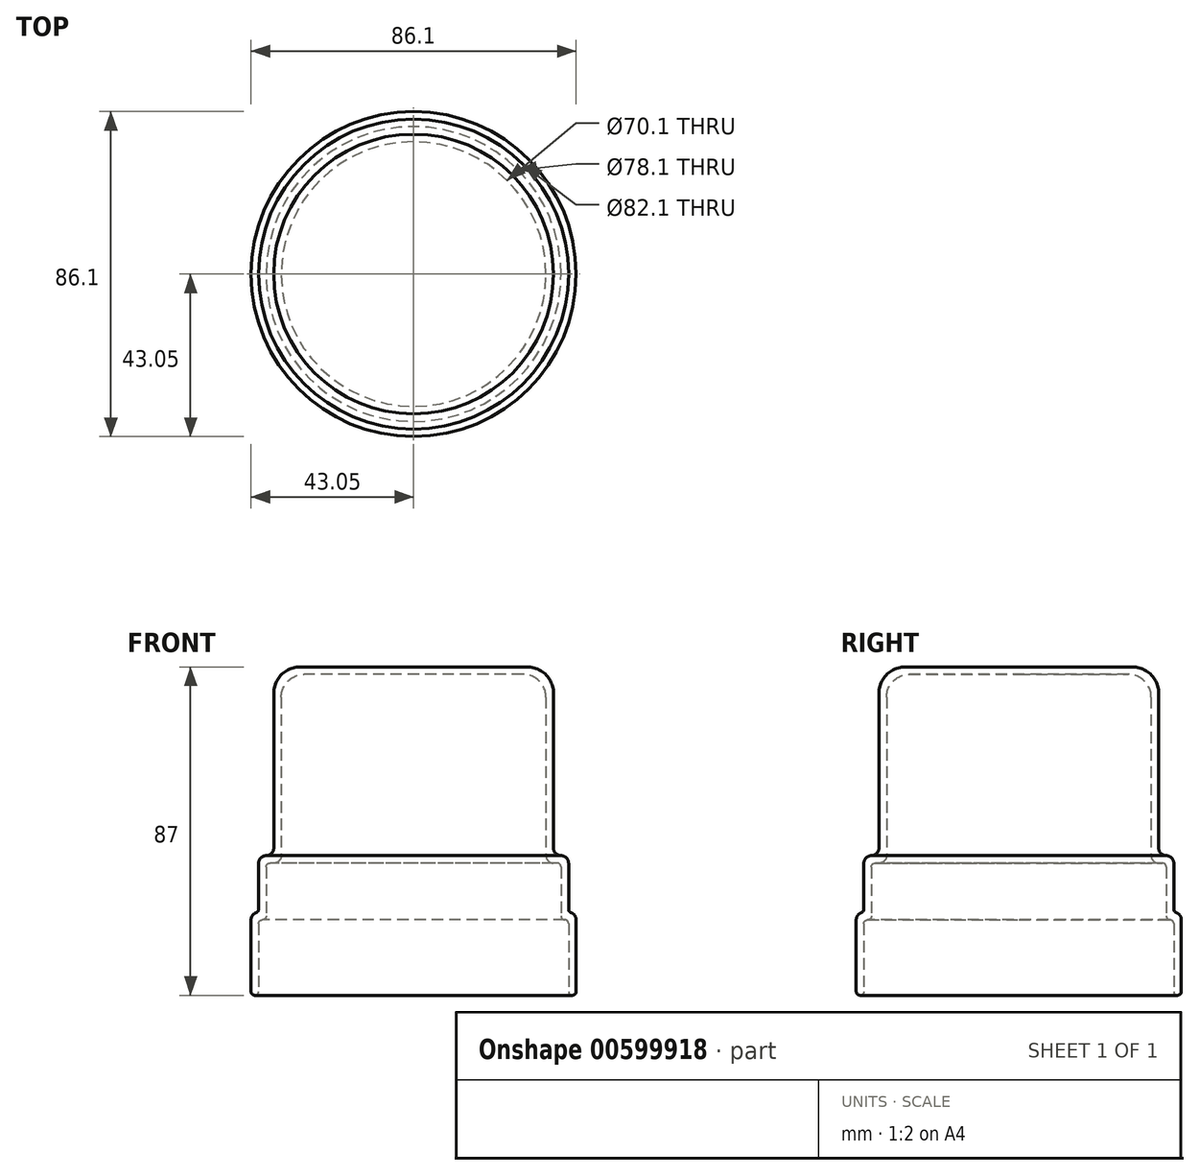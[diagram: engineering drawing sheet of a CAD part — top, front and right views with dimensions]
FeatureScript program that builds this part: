
annotation { "Feature Type Name" : "Feature", "Feature Type Description" : "" }
export const myFeature = defineFeature(function(context is Context, id is Id, definition is map)
    precondition{}
    {
        {
            var Q0;
            Q0=qCreatedBy(makeId("Front.planeOp"),FACE);
            var sketch = newSketch(context, id + "F0", { "sketchPlane" : qUnion([Q0])});
            skLineSegment(sketch, "E0", {"start": v(41.05, -10) * mm, "end": v(41.05, 10) * mm});
            skLineSegment(sketch, "E1", {"start": v(41.05, 10) * mm, "end": v(39.05, 10) * mm});
            skLineSegment(sketch, "E2", {"start": v(39.05, 10) * mm, "end": v(39.05, 25) * mm});
            skLineSegment(sketch, "E3", {"start": v(39.05, 25) * mm, "end": v(35.05, 25) * mm});
            skLineSegment(sketch, "E4", {"start": v(35.05, 25) * mm, "end": v(35.05, 75) * mm});
            skLineSegment(sketch, "E5", {"start": v(35.05, 75) * mm, "end": v(0, 75) * mm});
            skLineSegment(sketch, "E6.0", {"start": v(37.05, 77) * mm, "end": v(0, 77) * mm});
            skLineSegment(sketch, "E6.1", {"start": v(37.05, 27) * mm, "end": v(37.05, 77) * mm});
            skLineSegment(sketch, "E6.2", {"start": v(43.05, -10) * mm, "end": v(43.05, 12) * mm});
            skLineSegment(sketch, "E6.3", {"start": v(43.05, 12) * mm, "end": v(41.05, 12) * mm});
            skLineSegment(sketch, "E6.4", {"start": v(41.05, 12) * mm, "end": v(41.05, 27) * mm});
            skLineSegment(sketch, "E6.5", {"start": v(41.05, 27) * mm, "end": v(37.05, 27) * mm});
            skLineSegment(sketch, "E7", {"start": v(41.05, -10) * mm, "end": v(43.05, -10) * mm});
            skLineSegment(sketch, "E8", {"start": v(0, 75) * mm, "end": v(0, 77) * mm});
            skSolve(sketch);
        }
        {
            var Q0;
            Q0=makeQuery(id+"F0.imprint","IMPRINT",FACE,{"disambiguationData":[TD([[makeQuery(id+"F0.imprint","IMPRINT",EDGE,{"derivedFrom":sQuery(id+"F0.wireOp",EDGE,"E0")}),-1.0]])]});
            var Q1;
            Q1=sQuery(id+"F0.wireOp",EDGE,"E8");
            revolve(context, id + "F1", {"entities" : qUnion([Q0]), "axis" : qUnion([Q1]), "revolveType" : RevolveType.FULL});
        }
        {
            var Q0;
            Q0=makeQuery(id+"F1.opRevolve","SWEPT_EDGE",EDGE,{"disambiguationData":[OSD([sQuery(id+"F0.wireOp",EDGE,"E4"),sQuery(id+"F0.wireOp",EDGE,"E5")])]});
            fillet(context, id + "F2", {"entities" : qUnion([Q0]), "radius" : 6 * mm, "tangentPropagation" : true, "allowEdgeOverflow" : false});
        }
        {
            var Q0;
            Q0=makeQuery(id+"F1.opRevolve","SWEPT_EDGE",EDGE,{"disambiguationData":[OSD([sQuery(id+"F0.wireOp",EDGE,"E6.0"),sQuery(id+"F0.wireOp",EDGE,"E6.1")])]});
            fillet(context, id + "F3", {"entities" : qUnion([Q0]), "radius" : 7 * mm, "tangentPropagation" : true, "allowEdgeOverflow" : false});
        }
        {
            var Q0;
            Q0=makeQuery(id+"F1.opRevolve","SWEPT_EDGE",EDGE,{"disambiguationData":[OSD([sQuery(id+"F0.wireOp",EDGE,"E6.1"),sQuery(id+"F0.wireOp",EDGE,"E6.5")])]});
            var Q1;
            Q1=makeQuery(id+"F1.opRevolve","SWEPT_EDGE",EDGE,{"disambiguationData":[OSD([sQuery(id+"F0.wireOp",EDGE,"E6.2"),sQuery(id+"F0.wireOp",EDGE,"E6.3")])]});
            var Q2;
            Q2=makeQuery(id+"F1.opRevolve","SWEPT_EDGE",EDGE,{"disambiguationData":[OSD([sQuery(id+"F0.wireOp",EDGE,"E3"),sQuery(id+"F0.wireOp",EDGE,"E4")])]});
            fillet(context, id + "F4", {"entities" : qUnion([Q0, Q1, Q2]), "radius" : 2 * mm, "tangentPropagation" : true, "allowEdgeOverflow" : false});
        }
        {
            var Q0;
            Q0=makeQuery(id+"F1.opRevolve","SWEPT_EDGE",EDGE,{"disambiguationData":[OSD([sQuery(id+"F0.wireOp",EDGE,"E2"),sQuery(id+"F0.wireOp",EDGE,"E3")])]});
            var Q1;
            Q1=makeQuery(id+"F1.opRevolve","SWEPT_EDGE",EDGE,{"disambiguationData":[OSD([sQuery(id+"F0.wireOp",EDGE,"E0"),sQuery(id+"F0.wireOp",EDGE,"E1")])]});
            var Q2;
            Q2=makeQuery(id+"F1.opRevolve","SWEPT_EDGE",EDGE,{"disambiguationData":[OSD([sQuery(id+"F0.wireOp",EDGE,"E6.2"),sQuery(id+"F0.wireOp",EDGE,"E7")])]});
            var Q3;
            Q3=makeQuery(id+"F1.opRevolve","SWEPT_EDGE",EDGE,{"disambiguationData":[OSD([sQuery(id+"F0.wireOp",EDGE,"E0"),sQuery(id+"F0.wireOp",EDGE,"E7")])]});
            var Q4;
            Q4=makeQuery(id+"F4.opFillet","BLEND_EDGE",EDGE,{"blendedFrom":[makeQuery(id+"F1.opRevolve","SWEPT_EDGE",EDGE,{"disambiguationData":[OSD([sQuery(id+"F0.wireOp",EDGE,"E6.2"),sQuery(id+"F0.wireOp",EDGE,"E6.3")])]}),makeQuery(id+"F1.opRevolve","SWEPT_FACE",FACE,{"disambiguationData":[OSD([sQuery(id+"F0.wireOp",EDGE,"E6.4")])]})],"blendedInto":[makeQuery(id+"F1.opRevolve","SWEPT_FACE",FACE,{"disambiguationData":[OSD([sQuery(id+"F0.wireOp",EDGE,"E6.4")])]})]});
            fillet(context, id + "F5", {"entities" : qUnion([Q0, Q1, Q2, Q3, Q4]), "radius" : 1 * mm, "tangentPropagation" : true, "allowEdgeOverflow" : false});
        }
        {
            var Q0;
            Q0=makeQuery(id+"F1.opRevolve","SWEPT_EDGE",EDGE,{"disambiguationData":[OSD([sQuery(id+"F0.wireOp",EDGE,"E6.4"),sQuery(id+"F0.wireOp",EDGE,"E6.5")])]});
            fillet(context, id + "F6", {"entities" : qUnion([Q0]), "radius" : 2 * mm, "tangentPropagation" : true, "allowEdgeOverflow" : false});
        }
        {
            var Q0;
            Q0=makeQuery(id+"F1.opRevolve","SWEPT_EDGE",EDGE,{"disambiguationData":[OSD([sQuery(id+"F0.wireOp",EDGE,"E1"),sQuery(id+"F0.wireOp",EDGE,"E2")])]});
            fillet(context, id + "F7", {"entities" : qUnion([Q0]), "radius" : 1 * mm, "tangentPropagation" : true, "allowEdgeOverflow" : false});
        }
    });
